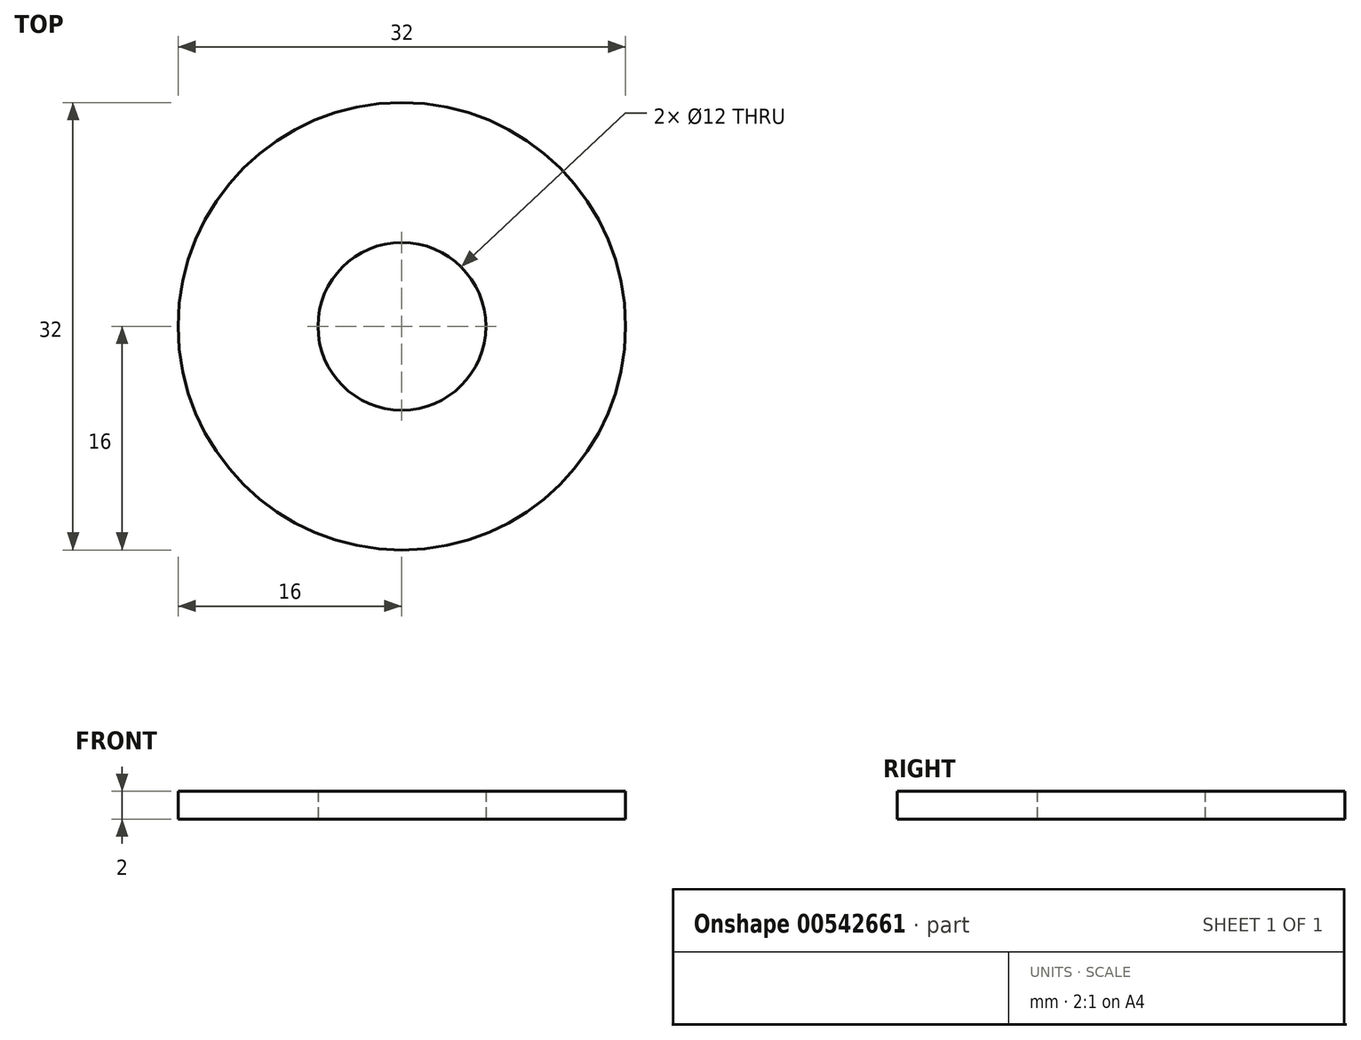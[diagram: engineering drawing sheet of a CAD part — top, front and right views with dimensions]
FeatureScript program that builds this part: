
annotation { "Feature Type Name" : "Feature", "Feature Type Description" : "" }
export const myFeature = defineFeature(function(context is Context, id is Id, definition is map)
    precondition{}
    {
        {
            var Q0;
            Q0=qCreatedBy(makeId("Top.planeOp"),FACE);
            var sketch = newSketch(context, id + "F0", { "sketchPlane" : qUnion([Q0])});
            skCircle(sketch, "E0", {"center": v(0, 0) * mm, "radius": 16 * mm});
            skSolve(sketch);
        }
        {
            var Q0;
            Q0=makeQuery(id+"F0.imprint","IMPRINT",FACE,{"disambiguationData":[TD([[makeQuery(id+"F0.imprint","IMPRINT",EDGE,{"derivedFrom":sQuery(id+"F0.wireOp",EDGE,"E0")}),1.0]])]});
            extrude(context, id + "F1", {"entities" : qUnion([Q0]), "depth" : 2 * mm, "offsetDistance" : 25 * mm});
        }
        {
            var Q0;
            Q0=qCreatedBy(makeId("Top.planeOp"),FACE);
            var sketch = newSketch(context, id + "F2", { "sketchPlane" : qUnion([Q0])});
            skCircle(sketch, "E1", {"center": v(0, 0) * mm, "radius": 6 * mm});
            skSolve(sketch);
        }
        {
            var Q0;
            Q0=qSketchRegion(id+"F2",true);
            extrude(context, id + "F3", {"entities" : qUnion([Q0]), "operationType" : NewBodyOperationType.REMOVE, "depth" : 25 * mm, "offsetDistance" : 25 * mm});
        }
    });
